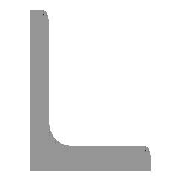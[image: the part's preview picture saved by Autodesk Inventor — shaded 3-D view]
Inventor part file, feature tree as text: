
AUTODESK INVENTOR PART (.ipt)
format: ipt  version: 2021 (Build 250183000, 183)  size: 116,736 bytes
history: native  units: mm (DEFAULTED — no unit token found)
features: other x3, sketch x2, extrude x1, plane x1
ambient origin geometry x8: Origin, YZ Plane, XZ Plane, XY Plane, X Axis, Y Axis, Z Axis, Center Point
bodies: Solid1 (feature_tree)
feature tree (7):
  other  "Driven Length"
  other  "Płaszczyzna początkowa"
  other  "Płaszczyzna końcowa"
  extrude  "Bryła"  Depth=25.0mm
  sketch  "Sketch3"  dims[d0=25.0mm d1=25.0mm]
  plane  "Work Plane3"
  sketch  "Sketch4"  dims[d2=3.0mm d3=3.0mm d4=2000.0mm d5=0.0mm d8=4.5mm d9=3.0mm d10=0.0mm d11=0.0mm d12=-0.0mm d13=2000.0mm d14=90.0deg d15=2000.0mm]
